# Revit family: Electronics_Desono_Biamp_Ceiling-Loudspeaker_CM20DTS
name_source: partatom
category: Communication Devices
units: mm (PartAtom-declared; Revit-internal decimal feet)

## family parameters
Cut with Voids When Loaded = No
Host = Face
Maintain Annotation Orientation = No
OmniClass Number = 23.85.10.11.14.14.14
OmniClass Title = Loudspeakers
Part Type = Normal
Room Calculation Point = No
Round Connector Dimension = Use Diameter
Shared = No

## types (1)
- CM20DTS
    Compliance = ETL listed to comply with UL 1480A and UL 2043;Certifed to CSA C22.2#62368-1;Suitable for use in air handling spaces per NFPA 70, NFPA 90;Conforms with City of Chicago Codes
    Connector Description = 4-way Euroblock; Low impedance 16 ohms, 70/100V operation
    Continuous Power Handling Nominal Impedance = 25V 40W @ 16Ω (160W peak)
    Cutout Diameter = 7.6 (193 mm)
    Default Elevation = 4' - 0"
    Depth = 0' - 3 1/2"
    Description = Desono™ CM20DTS Two-Way 4.25 Ceiling Loudspeaker
    Diameter = 0' - 9"
    Grill Material = Biamp - Plastic - Gray(Grid)
    Housing Material = Biamp - Plastic - Gray
    Input Connection = (1) 4-way Euroblock connector with permanent pass-through
    Manufacturer = Biamp
    Model = CM20DTS
    Mounting Provisions = 2 mounting clamps with grip range of 0.2 - 1.6 (3 - 41 mm);Cover plate with 0.75 (22 mm) NPT knockout for conduit connectors
    Nominal Beamwidth  (H x V) = 150° x 100°
    Nominal Maximum SPL @ 1m = Peak - 109dB; Continuous - 103dB
    Nominal Sensitivity @ 1m = 1W - 87dB;2.83V - 84dB
    Operating Environment = Indoor
    Operating Mode = Passive
    Operating Range (-10dB) = 90 Hz to 22 kHz
    Product Documentation Link = https://downloads.biamp.com
    Product Page URL = https://www.biamp.com
    Product data url = https://www.bimobject.com
    Protection = 3-step self-resetting protection
    Recommended Amplifers = 40W - 80W @ 16Ω (25V - 36V)
    Safety Features = 2 hang points
    Shipping Weight = 7.70 lb
    Transducers = LF 1 x 4.25 (108 mm) treated paper cone;HF 1 x 1 (25 mm) soft dome
    Transformer = 70V: 20W, 10W, 5W, 2.5W, 1.25W;100V: 20W, 10W, 5W, 2.5W
    URL = https://www.biamp.com
    Weight = 4.41 lb

## geometry (parser evidence)
native form markers: Sweep x8
no freeform markers — native parametric forms only
